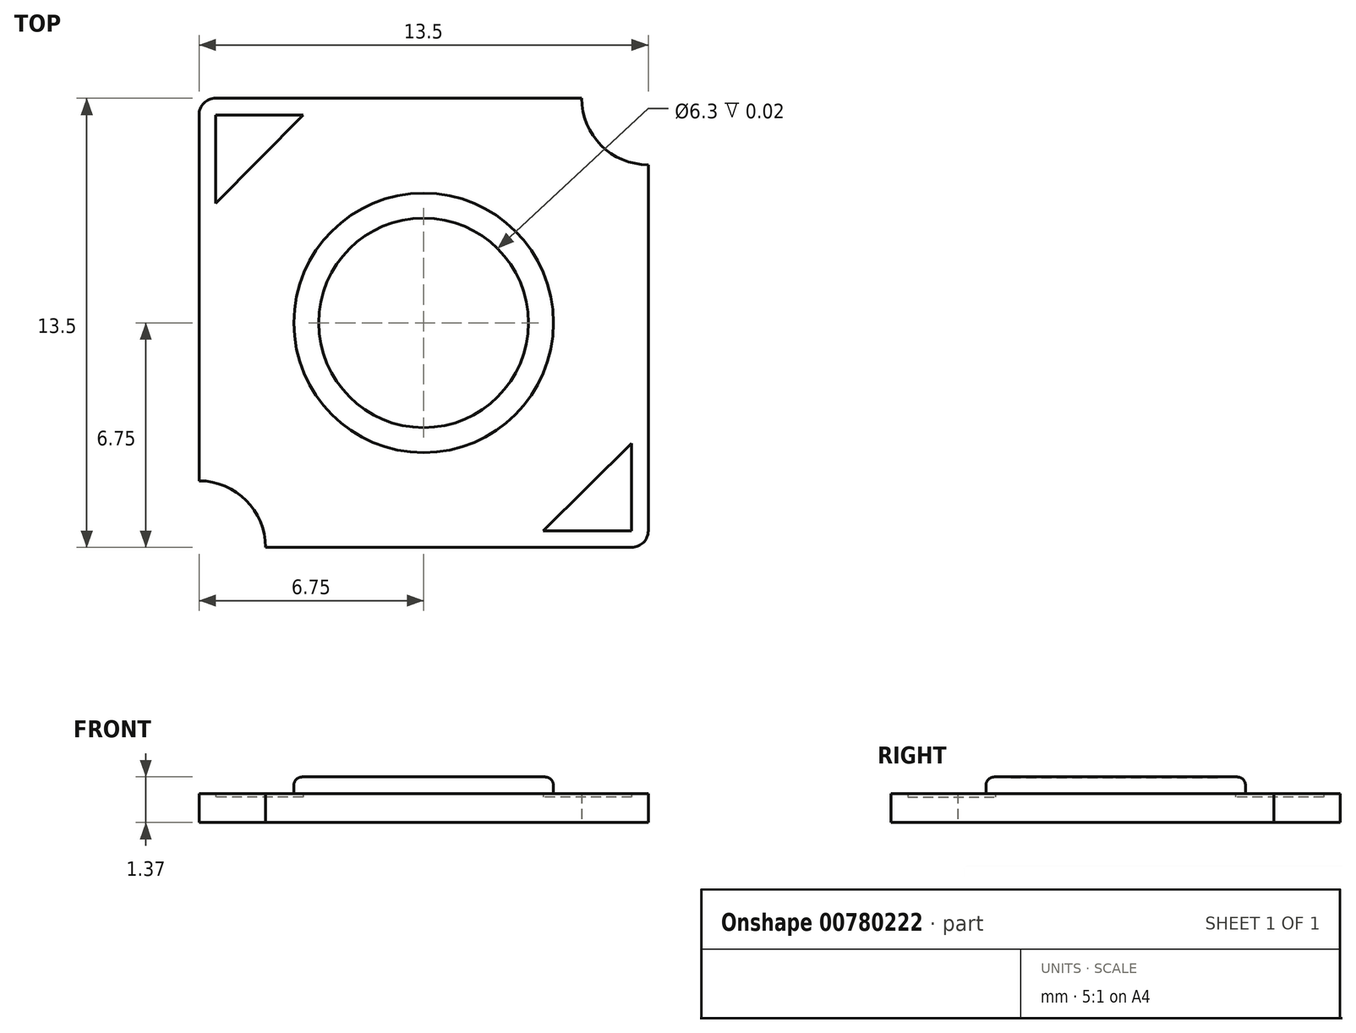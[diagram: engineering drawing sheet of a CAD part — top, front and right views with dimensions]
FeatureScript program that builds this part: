
annotation { "Feature Type Name" : "Feature", "Feature Type Description" : "" }
export const myFeature = defineFeature(function(context is Context, id is Id, definition is map)
    precondition{}
    {
        {
            var Q0;
            Q0=qCreatedBy(makeId("Top.planeOp"),FACE);
            var sketch = newSketch(context, id + "F0", { "sketchPlane" : qUnion([Q0])});
            skLineSegment(sketch, "E0.bottom", {"start": v(6.25, -6.75) * mm, "end": v(-6.75, -6.75) * mm});
            skLineSegment(sketch, "E0.top", {"start": v(6.75, 6.75) * mm, "end": v(-6.25, 6.75) * mm});
            skLineSegment(sketch, "E0.left", {"start": v(6.75, -6.25) * mm, "end": v(6.75, 6.75) * mm});
            skLineSegment(sketch, "E0.right", {"start": v(-6.75, -6.75) * mm, "end": v(-6.75, 6.25) * mm});
            skPoint(sketch, "E0.middle", {"position": v(0, 0) * mm});
            skCircle(sketch, "E1", {"center": v(6.75, 6.75) * mm, "radius": 2 * mm});
            skCircle(sketch, "E2", {"center": v(-6.75, -6.75) * mm, "radius": 2 * mm});
            skCircle(sketch, "E3", {"center": v(0, 0) * mm, "radius": 3.15 * mm});
            skCircle(sketch, "E4", {"center": v(0, 0) * mm, "radius": 3.9 * mm});
            skPoint(sketch, "E5.visualSharp", {"position": v(6.75, -6.75) * mm});
            skArc(sketch, "E5.filletArc", {"start": v(6.25, -6.75) * mm, "mid": v(6.6, -6.6) * mm, "end": v(6.75, -6.25) * mm});
            skPoint(sketch, "E6.visualSharp", {"position": v(-6.75, 6.75) * mm});
            skArc(sketch, "E6.filletArc", {"start": v(-6.25, 6.75) * mm, "mid": v(-6.6, 6.6) * mm, "end": v(-6.75, 6.25) * mm});
            skLineSegment(sketch, "E7", {"start": v(-6.25, 6.25) * mm, "end": v(-6.25, 3.6) * mm});
            skLineSegment(sketch, "E8", {"start": v(-6.25, 3.6) * mm, "end": v(-3.62, 6.25) * mm});
            skLineSegment(sketch, "E9", {"start": v(-3.62, 6.25) * mm, "end": v(-6.25, 6.25) * mm});
            skLineSegment(sketch, "E10.MirrorCS", {"start": v(3.6, -6.25) * mm, "end": v(6.25, -3.62) * mm});
            skLineSegment(sketch, "E11.MirrorCS", {"start": v(6.25, -3.62) * mm, "end": v(6.25, -6.25) * mm});
            skLineSegment(sketch, "E12.MirrorCS", {"start": v(6.25, -6.25) * mm, "end": v(3.6, -6.25) * mm});
            skSolve(sketch);
        }
        {
            var Q0;
            Q0=makeQuery(id+"F0.imprint","IMPRINT",FACE,{"disambiguationData":[TD([[makeQuery(id+"F0.imprint","IMPRINT",EDGE,{"derivedFrom":sQuery(id+"F0.wireOp",EDGE,"E4")}),-1.0]])]});
            var Q1;
            Q1=makeQuery(id+"F0.imprint","IMPRINT",FACE,{"disambiguationData":[TD([[makeQuery(id+"F0.imprint","IMPRINT",EDGE,{"derivedFrom":sQuery(id+"F0.wireOp",EDGE,"E3")}),-1.0]])]});
            var Q2;
            Q2=makeQuery(id+"F0.imprint","IMPRINT",FACE,{"disambiguationData":[TD([[makeQuery(id+"F0.imprint","IMPRINT",EDGE,{"derivedFrom":sQuery(id+"F0.wireOp",EDGE,"E3")}),1.0]])]});
            extrude(context, id + "F1", {"entities" : qUnion([Q0, Q1, Q2]), "depth" : .87 * mm, "offsetDistance" : 25 * mm});
        }
        {
            var Q0;
            Q0=makeQuery(id+"F0.imprint","IMPRINT",FACE,{"disambiguationData":[TD([[makeQuery(id+"F0.imprint","IMPRINT",EDGE,{"derivedFrom":sQuery(id+"F0.wireOp",EDGE,"E7")}),1.0]])]});
            var Q1;
            Q1=makeQuery(id+"F0.imprint","IMPRINT",FACE,{"disambiguationData":[TD([[makeQuery(id+"F0.imprint","IMPRINT",EDGE,{"derivedFrom":sQuery(id+"F0.wireOp",EDGE,"E10.MirrorCS")}),-1.0]])]});
            extrude(context, id + "F2", {"entities" : qUnion([Q0, Q1]), "operationType" : NewBodyOperationType.ADD, "depth" : .77 * mm, "offsetDistance" : 25 * mm});
        }
        {
            var Q0;
            Q0=makeQuery(id+"F0.imprint","IMPRINT",FACE,{"disambiguationData":[TD([[makeQuery(id+"F0.imprint","IMPRINT",EDGE,{"derivedFrom":sQuery(id+"F0.wireOp",EDGE,"E3")}),-1.0]])]});
            extrude(context, id + "F3", {"entities" : qUnion([Q0]), "operationType" : NewBodyOperationType.ADD, "depth" : 1.37 * mm, "offsetDistance" : 25 * mm});
        }
        {
            var Q0;
            Q0=makeQuery(id+"F0.imprint","IMPRINT",FACE,{"disambiguationData":[TD([[makeQuery(id+"F0.imprint","IMPRINT",EDGE,{"derivedFrom":sQuery(id+"F0.wireOp",EDGE,"E3")}),1.0]])]});
            extrude(context, id + "F4", {"entities" : qUnion([Q0]), "operationType" : NewBodyOperationType.ADD, "depth" : 1.35 * mm, "offsetDistance" : 25 * mm});
        }
        {
            var Q0;
            Q0=makeQuery(id+"F3.opExtrude","CAP_EDGE",EDGE,{"disambiguationData":[OSD([sQuery(id+"F0.wireOp",EDGE,"E4")])],"isStart":false});
            fillet(context, id + "F5", {"entities" : qUnion([Q0]), "radius" : .25 * mm, "tangentPropagation" : true, "allowEdgeOverflow" : false});
        }
    });
